# Revit family: FAUCET (90)
name_source: partatom
category: Plumbing Fixtures
units: mm (PartAtom-declared; Revit-internal decimal feet)

## family parameters
Always vertical = Yes
Cut with Voids When Loaded = No
OmniClass Number = 23.45.55.17
OmniClass Title = Mixing Faucets
Part Type = Normal
Room Calculation Point = No
Round Connector Dimension = Use Radius
Shared = No
Work Plane-Based = No

## types (1)
- FAUCET (90)
    ADA Compliant = Yes
    Assembly Code = D2010900
    CADworks URL = http://www.CADworks.net
    CW Connection = Yes
    CWFU = 0
    Cold Water Connection NPT = 0"
    Cold Water Connection Radius = 0' - 0 3/16"
    Default Elevation = 0' - 0"
    Description = Three Handle Bidet Faucet
    Finish = Bronze-Brizo-Metal-Brilliance-Brushed
    HW Connection = Yes
    HWFU = 0
    Hot Water Connection NPT = 0"
    Hot Water Connection Radius = 0' - 0 3/16"
    Manufacturer = Brizo
    Model = 68414-BZ
    Nominal Height = 0' - 5 3/8"
    Product URL = http://www.brizo.com
    Series = Quiessence
    URL = http://www.brizo.com
    Vent Connection = Yes
    WFU = 0
    Waste Connection = Yes

## geometry (parser evidence)
native form markers: Sweep x1
no freeform markers — native parametric forms only
